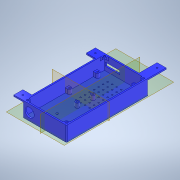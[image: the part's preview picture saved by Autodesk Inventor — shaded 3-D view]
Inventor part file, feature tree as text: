
AUTODESK INVENTOR PART (.ipt)
format: ipt  version: 2022 (Build 260153000, 153)  size: 416,768 bytes
history: native  units: in
note: dims shown in document units (in); Inventor stores cm internally (conversion verified against a paired STEP export)
features: reference x15, extrude x12, sketch x12, projected_geometry x5, other x5, plane x3, mirror x2, pattern_linear x1, hole x1, chamfer x1, fillet x1
ambient origin geometry x8: Origin, YZ Plane, XZ Plane, XY Plane, X Axis, Y Axis, Z Axis, Center Point
bodies: Body1 (feature_tree)
feature tree (58):
  plane  "Work Plane2"
  extrude  "Extrusion14"  Depth=0.7874in
  extrude  "Extrusion15"  Depth=0.1181in TaperAngle=0.0deg
  extrude  "Extrusion17"  Depth=1.1811in TaperAngle=0.0deg
  extrude  "Extrusion18"  Depth=0.1575in
  extrude  "Extrusion19"  Depth=0.3937in TaperAngle=0.0deg
  pattern_linear  "Rectangular Pattern1"  Count1=8 Spacing1=0.3937in
  extrude  "Extrusion20"  Depth=0.3937in
  extrude  "Extrusion21"  Depth=0.3937in TaperAngle=0.0deg
  extrude  "Extrusion22"  Depth=0.0787in
  extrude  "Extrusion23"  Depth=0.0787in
  hole  "Hole19"  [1 undecoded]
  sketch  "Sketch32"  dims[d136=1.9685in d138=0.3937in d139=0.5906in]
  extrude  "Extrusion24"  Depth=0.0787in
  extrude  "Extrusion25"  Depth=0.3937in TaperAngle=0.0deg
  plane  "Work Plane3"
  plane  "Work Plane4"
  mirror  "Mirror1"
  mirror  "Mirror2"
  chamfer  "Chamfer2"  Distance=0.3937in
  fillet  "Fillet2"  Radius=1.5748in
  extrude  "Extrusion26"  Depth=0.1181in TaperAngle=0.0deg
  sketch  "Sketch22"  dims[d108=0.2756in d109=0.7874in]
  reference  "Reference1"
  reference  "Reference2"
  reference  "Reference3"
  sketch  "Sketch23"  dims[d111=0.7874in d112=0.1181in d113=0.0in]
  projected_geometry  "Projected Loop2"
  sketch  "Sketch24"  dims[d114=0.1181in d115=1.1811in d116=0.0in]
  reference  "Reference4"
  reference  "Reference5"
  reference  "Reference6"
  reference  "Reference7"
  reference  "Reference8"
  sketch  "Sketch25"  dims[d117=0.1969in d122=0.1575in]
  projected_geometry  "Projected Loop3"
  sketch  "Sketch26"  dims[d123=0.315in d124=0.3937in d125=0.0in]
  sketch  "Sketch27"  dims[d126=0.1575in d127=0.0in]
  projected_geometry  "Projected Loop4"
  sketch  "Sketch28"  dims[d128=0.1181in]
  reference  "Reference9"
  reference  "Reference10"
  reference  "Reference11"
  reference  "Reference12"
  reference  "Reference13"
  sketch  "Sketch29"  dims[d129=0.7283in]
  projected_geometry  "Projected Loop5"
  sketch  "Sketch30"  dims[d130=0.9843in]
  sketch  "Sketch31"  dims[d131=0.3937in d132=0.0in d133=3.1496in d135=0.3937in]
  projected_geometry  "Projected Loop6"
  sketch  "Sketch33"  dims[d140=0.7874in d141=0.3937in d142=0.0in d143=0.0787in d144=0.0787in d145=0.0787in d146=0.0787in d147=0.3937in d148=0.0in d149=0.3937in d150=0.0in d151=1.5748in d152=0.1181in d153=0.0in d154=0.126in d155=0.2362in d156=0.119in d157=0.0787in d158=0.563in d159=0.315in d160=0.8108in d161=0.1969in d162=0.0787in d163=0.0787in d164=0.0in d165=0.0689in d166=0.0in d170=0.2236in d171=0.0787in d172=45.0deg d173=0.0787in d174=0.7874in d175=0.0in d176=0.0in]
  reference  "Reference14"
  reference  "Reference15"
  parser-record x1  (decoder bookkeeping rows leaked as tree rows — omitted from the tree; the rows remain in map.json)
  other  "Electronics Box.iam"
  other  "SKR MINI E3 V1.2:1"
  other  "SSR-40:1"
  other  "SKR Mini E3 v2.0:1"
note: 1 required parameter value undecoded (feature->parameter linkage not recoverable at this tier; creation-order binding heuristic only, values carry confidence <= 0.55)
note: 1 file-system path scrubbed to <path> (originals preserved in map.json)
